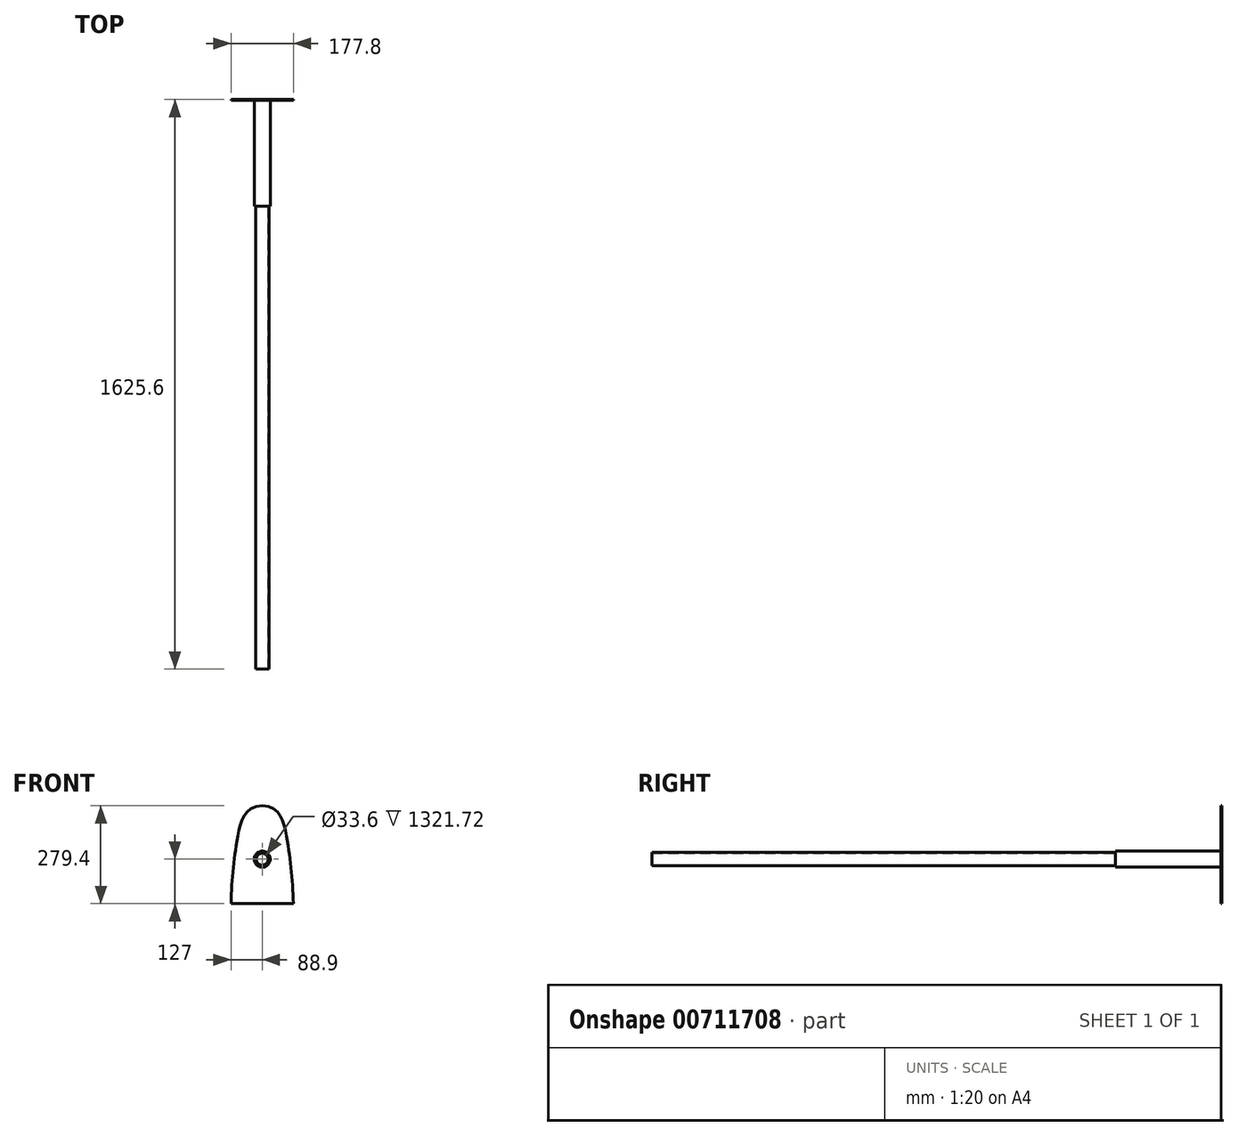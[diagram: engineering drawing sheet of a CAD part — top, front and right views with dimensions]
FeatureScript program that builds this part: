
annotation { "Feature Type Name" : "Feature", "Feature Type Description" : "" }
export const myFeature = defineFeature(function(context is Context, id is Id, definition is map)
    precondition{}
    {
        {
            var Q0;
            Q0=qCreatedBy(makeId("Front.planeOp"),FACE);
            var sketch = newSketch(context, id + "F0", { "sketchPlane" : qUnion([Q0])});
            skLineSegment(sketch, "E0.bottom", {"start": v(-88.9, 279.4) * mm, "end": v(88.9, 279.4) * mm, "construction": true});
            skLineSegment(sketch, "E0.top", {"start": v(-88.9, 0) * mm, "end": v(88.9, 0) * mm, "construction": true});
            skLineSegment(sketch, "E0.left", {"start": v(-88.9, 279.4) * mm, "end": v(-88.9, 0) * mm, "construction": true});
            skLineSegment(sketch, "E0.right", {"start": v(88.9, 279.4) * mm, "end": v(88.9, 0) * mm, "construction": true});
            skLineSegment(sketch, "E1", {"start": v(-88.9, 0) * mm, "end": v(88.9, 0) * mm});
            skLineSegment(sketch, "E2", {"start": v(0, 0) * mm, "end": v(0, 279.4) * mm, "construction": true});
            skFitSpline(sketch, "E3", {"points": [v(-88.9, 0) * mm, v(-82.58, 97.77) * mm, v(-69.4, 193.95) * mm, v(0, 279.4) * mm], "startDerivative": vector(3.05, 300.32) * mm, "endDerivative": vector(453.14, 0) * mm});
            skFitSpline(sketch, "E4.MirrorCS", {"points": [v(88.9, 0) * mm, v(82.58, 97.77) * mm, v(69.4, 193.95) * mm, v(0, 279.4) * mm], "startDerivative": vector(-3.05, 300.32) * mm, "endDerivative": vector(-453.14, 0) * mm});
            skSolve(sketch);
        }
        {
            var Q0;
            Q0=makeQuery(id+"F0.imprint","IMPRINT",FACE,{"disambiguationData":[TD([[makeQuery(id+"F0.imprint","IMPRINT",EDGE,{"derivedFrom":sQuery(id+"F0.wireOp",EDGE,"E1")}),1.0]])]});
            extrude(context, id + "F1", {"entities" : qUnion([Q0]), "oppositeDirection" : true, "depth" : 2.25 * mm, "offsetDistance" : 25.4 * mm});
        }
        {
            var Q0;
            Q0=makeQuery(id+"F1.opExtrude","CAP_FACE",FACE,{"disambiguationData":[OSD([sQuery(id+"F0.wireOp",EDGE,"E1"),sQuery(id+"F0.wireOp",EDGE,"E3"),sQuery(id+"F0.wireOp",EDGE,"E4.MirrorCS")])],"isStart":false});
            var sketch = newSketch(context, id + "F2", { "sketchPlane" : qUnion([Q0])});
            skCircle(sketch, "E5", {"center": v(0, 127) * mm, "radius": 19.05 * mm});
            skCircle(sketch, "E6.0", {"center": v(0, 127) * mm, "radius": 16.8 * mm});
            skSolve(sketch);
        }
        {
            var Q0;
            Q0 = qSketchRegion(id + "F2", true);
            extrude(context, id + "F3", {"entities" : qUnion([Q0]), "operationType" : NewBodyOperationType.ADD, "oppositeDirection" : true, "depth" : 1625.6 * mm, "offsetDistance" : 25.4 * mm});
        }
        {
            var Q0;
            {var subQ0=sQuery(id+"F0.wireOp",EDGE,"E1");var subQ1=sQuery(id+"F0.wireOp",EDGE,"E3");var subQ2=sQuery(id+"F0.wireOp",EDGE,"E4.MirrorCS");Q0=makeQuery(id+"F3.boolean.opBoolean","SPLIT",FACE,{"disambiguationData":[TD([makeQuery(id+"F1.opExtrude","SWEPT_FACE",FACE,{"disambiguationData":[OSD([subQ0])]})])],"derivedFrom":makeQuery(id+"F1.opExtrude","CAP_FACE",FACE,{"disambiguationData":[OSD([subQ0,subQ1,subQ2])],"isStart":true})});}
            var Q1;
            Q1=makeQuery(id+"F3.opExtrude","CAP_FACE",FACE,{"disambiguationData":[OSD([sQuery(id+"F2.wireOp",EDGE,"E5"),sQuery(id+"F2.wireOp",EDGE,"E6.0")])],"isStart":false});
            cPlane(context, id + "F4", {"entities" : qUnion([Q0, Q1]), "cplaneType" : CPlaneType.MID_PLANE, "offset" : 25.4 * mm, "width" : 152.4 * mm, "height" : 152.4 * mm});
        }
        {
            var Q0;
            {var subQ0=sQuery(id+"F0.wireOp",EDGE,"E1");var subQ1=sQuery(id+"F0.wireOp",EDGE,"E3");var subQ2=sQuery(id+"F0.wireOp",EDGE,"E4.MirrorCS");Q0=makeQuery(id+"F3.boolean.opBoolean","SPLIT",FACE,{"disambiguationData":[TD([makeQuery(id+"F1.opExtrude","SWEPT_FACE",FACE,{"disambiguationData":[OSD([subQ0])]})])],"derivedFrom":makeQuery(id+"F1.opExtrude","CAP_FACE",FACE,{"disambiguationData":[OSD([subQ0,subQ1,subQ2])],"isStart":true})});}
            var sketch = newSketch(context, id + "F5", { "sketchPlane" : qUnion([Q0])});
            skCircle(sketch, "E7", {"center": v(0, 127) * mm, "radius": 22.86 * mm});
            skSolve(sketch);
        }
        {
            var Q0;
            Q0 = qSketchRegion(id + "F5", true);
            extrude(context, id + "F6", {"entities" : qUnion([Q0]), "operationType" : NewBodyOperationType.ADD, "depth" : 301.62 * mm, "offsetDistance" : 25.4 * mm});
        }
    });
